# Revit family: 2061003 Sylvania Lighting Fixture TubiXx LED pendant 2700K white-black
name_source: partatom
category: Lighting Fixtures
revit_build: Autodesk Revit 2016 (Build: 20150220_1215(x64)
units: mm (PartAtom-declared; Revit-internal decimal feet)

## family parameters
Cut with Voids When Loaded = No
Host = Face
Light Source = Yes
OmniClass Number = 23.80.70.00
OmniClass Title = Lighting
Part Type = Normal
Room Calculation Point = No
Round Connector Dimension = Use Diameter
Shared = No

## types (1)
- 2061003 TUBIXX LED PENDANT 2700K WHITE-BLACK
    Apparent Load = 14 VA
    Assembly Code = D5020200
    AssetType = Fixed
    Cable Length = 1500 mm
    Ceiling Rose Depth = 30 mm  [stored 0.0984252 ft]
    ClassificationName = Uniclass2015
    ClassificationValue = EF_70_80
    Color Filter = 16777215
    Cost = 0 $
    Default Elevation = 1219 mm
    Description = TubiXx LED Pendant is a decorative pendant fixture with integrated driver, equipped with an integrated non-dimmable LED driver, White finish with Black reflector, colour temperature 2700K, 14W, 1138lm, 81lm/W, IP20, IK02, Class I. Dimensions 250mmx80mm.
    Dimming Lamp Color Temperature Shift = <None>
    DocumentationLiterature = http://www.sylvania-lighting.com
    DurationUnit = hours
    ElectricShockClassification = 81
    Emit Shape Visible in Rendering = No
    Emit from Circle Diameter = 610 mm
    ExpectedLife = 50000
    IfcExportAs = Class I
    IfcExportType = IfcLightFixtureType
    ImpactProtectionIndex = IfcLightFixtureType
    IngressProtection = IfcLightFixtureType
    InputNominalFrequency = 2700
    InputVoltage = 0
    LampColourRenderingIndex = 16500
    LampColourTemperature = LED
    LampMacAdamStep = 92
    LampNominalLuminous = 2700 K
    LightOutputRatio = LED
    LuminaireType = 0
    ManufacturerName = 81 lm/W
    Material = Feilo Sylvania
    Material_1_FEILO = <By Category>
    Material_2_FEILO = <By Category>
    Material_3_FEILO = <By Category>
    Material_4_FEILO = <By Category>
    Model = TubiXx LED pendant 2700K white-black
    ModelNumber = 2061003
    ModelReference = TubiXx LED pendant 2700K white-black
    Name = TubiXx LED pendant 2700K white-black
    NominalDepth = 0 mm  [stored 0 ft]
    NominalHeight = 0 mm  [stored 0 ft]
    NominalLength = 0 mm  [stored 0 ft]
    Photometric Web File = 2061003.ies
    PowerConsumption = Lighting
    PowerFactor = 0
    Recess Depth = 28 mm
    Tilt Angle = 90.00°
    Tube Diameter = 80 mm  [stored 0.262467 ft]
    Tube Length = 250 mm  [stored 0.82021 ft]
    Type Image = <None>
    TypeName = TubiXx LED pendant 2700K white-black
    URL = 0.95
    Voltage = 0 V
    WarrantyDescription = http://www.sylvania-lighting.com

note: [stored X ft] marks values corroborated as IEEE doubles in the binary element streams (Revit-internal decimal feet)

## geometry (parser evidence)
native form markers: Sweep x2
no freeform markers — native parametric forms only
